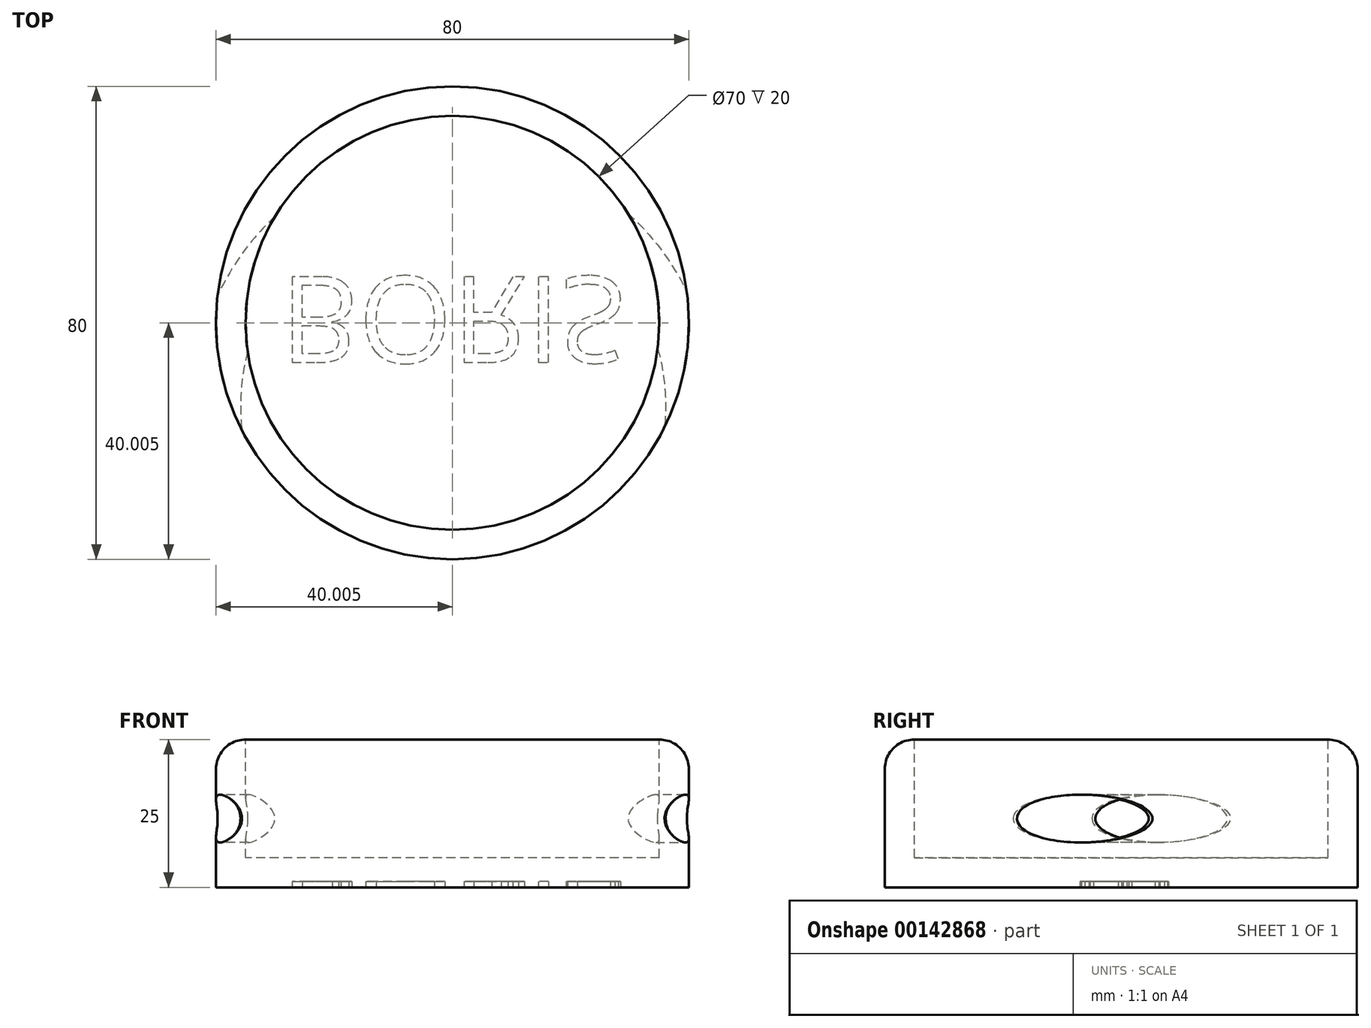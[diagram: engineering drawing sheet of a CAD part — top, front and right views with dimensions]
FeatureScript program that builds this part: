
annotation { "Feature Type Name" : "Feature", "Feature Type Description" : "" }
export const myFeature = defineFeature(function(context is Context, id is Id, definition is map)
    precondition{}
    {
        {
            var Q0;
            Q0=qCreatedBy(makeId("Top.planeOp"),FACE);
            var sketch = newSketch(context, id + "F0", { "sketchPlane" : qUnion([Q0])});
            skCircle(sketch, "E0", {"center": v(-1.27, 14.11) * mm, "radius": 40 * mm});
            skSolve(sketch);
        }
        {
            var Q0;
            Q0=makeQuery(id+"F0.imprint","IMPRINT",FACE,{"disambiguationData":[TD([[makeQuery(id+"F0.imprint","IMPRINT",EDGE,{"derivedFrom":sQuery(id+"F0.wireOp",EDGE,"E0")}),1.0]])]});
            extrude(context, id + "F1", {"entities" : qUnion([Q0]), "depth" : 25 * mm});
        }
        {
            var Q0;
            Q0=makeQuery(id+"F1.opExtrude","CAP_FACE",FACE,{"disambiguationData":[OSD([sQuery(id+"F0.wireOp",EDGE,"E0")])],"isStart":false});
            var sketch = newSketch(context, id + "F2", { "sketchPlane" : qUnion([Q0])});
            skCircle(sketch, "E1", {"center": v(-1.27, 14.11) * mm, "radius": 35 * mm});
            skSolve(sketch);
        }
        {
            var Q0;
            Q0=makeQuery(id+"F2.imprint","IMPRINT",FACE,{"disambiguationData":[TD([[makeQuery(id+"F2.imprint","IMPRINT",EDGE,{"derivedFrom":sQuery(id+"F2.wireOp",EDGE,"E1")}),1.0]])]});
            extrude(context, id + "F3", {"entities" : qUnion([Q0]), "operationType" : NewBodyOperationType.REMOVE, "oppositeDirection" : true, "depth" : 20 * mm});
        }
        {
            var Q0;
            Q0=makeQuery(id+"F1.opExtrude","CAP_EDGE",EDGE,{"disambiguationData":[OSD([sQuery(id+"F0.wireOp",EDGE,"E0")])],"isStart":false});
            fillet(context, id + "F4", {"entities" : qUnion([Q0]), "radius" : 5 * mm, "tangentPropagation" : true, "allowEdgeOverflow" : false});
        }
        {
            var Q0;
            Q0=qCreatedBy(makeId("Front.planeOp"),FACE);
            var sketch = newSketch(context, id + "F5", { "sketchPlane" : qUnion([Q0])});
            skCircle(sketch, "E2", {"center": v(-41.15, 11.63) * mm, "radius": 4.04 * mm});
            skLineSegment(sketch, "E3", {"start": v(-1.15, 29.71) * mm, "end": v(-1.15, 0.1) * mm});
            skSolve(sketch);
        }
        {
            var Q0;
            Q0=makeQuery(id+"F5.imprint","IMPRINT",FACE,{"disambiguationData":[TD([[makeQuery(id+"F5.imprint","IMPRINT",EDGE,{"derivedFrom":sQuery(id+"F5.wireOp",EDGE,"E2")}),1.0]])]});
            var Q1;
            Q1=sQuery(id+"F5.wireOp",EDGE,"E3");
            revolve(context, id + "F6", {"operationType" : NewBodyOperationType.REMOVE, "entities" : qUnion([Q0]), "axis" : qUnion([Q1]), "revolveType" : RevolveType.FULL, "oppositeDirection" : true});
        }
        {
            var Q0;
            Q0=makeQuery(id+"F1.opExtrude","CAP_FACE",FACE,{"disambiguationData":[OSD([sQuery(id+"F0.wireOp",EDGE,"E0")])],"isStart":true});
            var sketch = newSketch(context, id + "F7", { "sketchPlane" : qUnion([Q0])});
            skText(sketch, "E4", { "text": "BORIS", "fontName": "OpenSans-Regular.ttf"});
            const initialGuessF7  = {"E4": [-0.03036, -0.02193, 1, 0, 0.01466]};
            skSetInitialGuess(sketch, initialGuessF7);
            skSolve(sketch);
        }
        {
            var Q0;
            Q0 = qSketchRegion(id + "F7", true);
            extrude(context, id + "F8", {"entities" : qUnion([Q0]), "operationType" : NewBodyOperationType.REMOVE, "oppositeDirection" : true, "depth" : 1 * mm});
        }
    });
